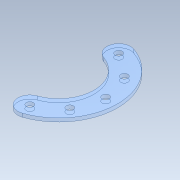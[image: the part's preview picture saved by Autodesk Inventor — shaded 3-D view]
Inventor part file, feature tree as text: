
AUTODESK INVENTOR PART (.ipt)
format: ipt  version: 2022 (Build 260153000, 153)  size: 157,696 bytes
history: native  units: mm
features: sketch x2, extrude x1
ambient origin geometry x8: Origin, YZ Plane, XZ Plane, XY Plane, X Axis, Y Axis, Z Axis, Center Point
bodies: Solid1 (feature_tree)
feature tree (3):
  sketch  "3D Sketch1"
  extrude  "Extrusion1"  [1 undecoded]
  sketch  "Sketch8"  dims[d1=3.0mm d2=0.0mm]
note: 1 required parameter value undecoded (feature->parameter linkage not recoverable at this tier; creation-order binding heuristic only, values carry confidence <= 0.55)
